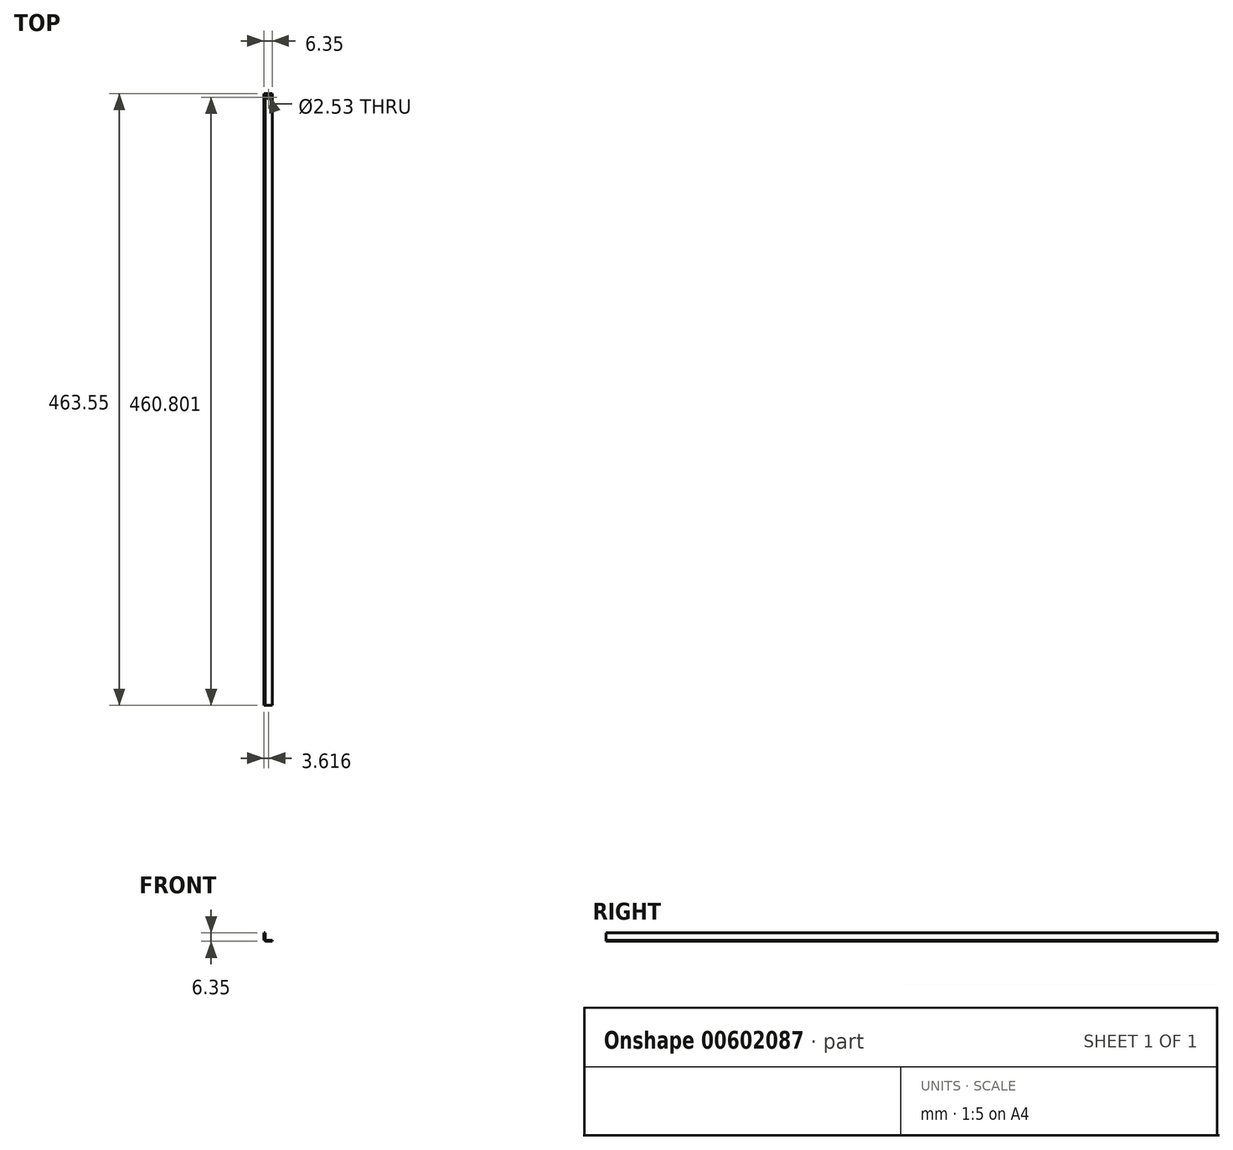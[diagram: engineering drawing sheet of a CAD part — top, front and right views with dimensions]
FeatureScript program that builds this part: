
annotation { "Feature Type Name" : "Feature", "Feature Type Description" : "" }
export const myFeature = defineFeature(function(context is Context, id is Id, definition is map)
    precondition{}
    {
        {
            var Q0;
            Q0=qCreatedBy(makeId("Front.planeOp"),FACE);
            var sketch = newSketch(context, id + "F0", { "sketchPlane" : qUnion([Q0])});
            skLineSegment(sketch, "E0.bottom", {"start": v(0, 0) * mm, "end": v(0.88, 0) * mm});
            skLineSegment(sketch, "E0.top", {"start": v(0, 6.35) * mm, "end": v(0.88, 6.35) * mm});
            skLineSegment(sketch, "E0.left", {"start": v(0, 0) * mm, "end": v(0, 6.35) * mm});
            skLineSegment(sketch, "E0.right", {"start": v(0.88, 0) * mm, "end": v(0.88, 6.35) * mm});
            skLineSegment(sketch, "E1.bottom", {"start": v(0, 0) * mm, "end": v(6.35, 0) * mm});
            skLineSegment(sketch, "E1.top", {"start": v(0, 0.81) * mm, "end": v(6.35, 0.81) * mm});
            skLineSegment(sketch, "E1.left", {"start": v(0, 0) * mm, "end": v(0, 0.81) * mm});
            skLineSegment(sketch, "E1.right", {"start": v(6.35, 0) * mm, "end": v(6.35, 0.81) * mm});
            skSolve(sketch);
        }
        {
            var Q0;
            {var subQ0=sQuery(id+"F0.wireOp",EDGE,"E0.top");Q0=makeQuery(id+"F0.imprint","IMPRINT",FACE,{"disambiguationData":[TD([[makeQuery(id+"F0.imprint","IMPRINT",EDGE,{"derivedFrom":subQ0}),-1.0]])]});}
            var Q1;
            {var subQ5=sQuery(id+"F0.wireOp",EDGE,"E1.right");Q1=makeQuery(id+"F0.imprint","IMPRINT",FACE,{"disambiguationData":[TD([[makeQuery(id+"F0.imprint","IMPRINT",EDGE,{"derivedFrom":subQ5}),1.0]])]});}
            var Q2;
            {var subQ5=sQuery(id+"F0.wireOp",EDGE,"E1.left");Q2=makeQuery(id+"F0.imprint","IMPRINT",FACE,{"disambiguationData":[TD([[makeQuery(id+"F0.imprint","IMPRINT",EDGE,{"derivedFrom":subQ5}),-1.0]])]});}
            extrude(context, id + "F1", {"entities" : qUnion([Q0, Q1, Q2]), "depth" : 463.55 * mm, "offsetDistance" : 25.4 * mm});
        }
        {
            var Q0;
            Q0=makeQuery(id+"F1.opExtrude","SWEPT_FACE",FACE,{"disambiguationData":[OSD([sQuery(id+"F0.wireOp",EDGE,"E1.top")])]});
            var sketch = newSketch(context, id + "F2", { "sketchPlane" : qUnion([Q0])});
            skLineSegment(sketch, "E2", {"start": v(0.88, 0) * mm, "end": v(3.62, 0) * mm});
            skLineSegment(sketch, "E3", {"start": v(0.88, 0) * mm, "end": v(0.88, -2.75) * mm});
            skCircle(sketch, "E4", {"center": v(3.62, -2.75) * mm, "radius": 1.26 * mm});
            skSolve(sketch);
        }
        {
            var Q0;
            Q0=makeQuery(id+"F2.imprint","IMPRINT",FACE,{"disambiguationData":[TD([[makeQuery(id+"F2.imprint","IMPRINT",EDGE,{"derivedFrom":sQuery(id+"F2.wireOp",EDGE,"E4")}),1.0]])]});
            extrude(context, id + "F3", {"entities" : qUnion([Q0]), "operationType" : NewBodyOperationType.REMOVE, "oppositeDirection" : true, "depth" : 25.4 * mm, "offsetDistance" : 25.4 * mm});
        }
        {
            var Q0;
            Q0=makeQuery(id+"F1.opExtrude","SWEPT_FACE",FACE,{"disambiguationData":[OSD([sQuery(id+"F0.wireOp",EDGE,"E1.top")])]});
            var sketch = newSketch(context, id + "F4", { "sketchPlane" : qUnion([Q0])});
            skLineSegment(sketch, "E5", {"start": v(6.35, -463.55) * mm, "end": v(6.35, -460.8) * mm});
            skCircle(sketch, "E6", {"center": v(3.62, -460.8) * mm, "radius": 1.28 * mm});
            skPoint(sketch, "E6.centerSnap0", {"position": v(3.62, -463.55) * mm});
            skSolve(sketch);
        }
        {
            var Q0;
            Q0=makeQuery(id+"F4.imprint","IMPRINT",FACE,{"disambiguationData":[TD([[makeQuery(id+"F4.imprint","IMPRINT",EDGE,{"derivedFrom":sQuery(id+"F4.wireOp",EDGE,"E6")}),1.0]])]});
            extrude(context, id + "F5", {"entities" : qUnion([Q0]), "operationType" : NewBodyOperationType.REMOVE, "oppositeDirection" : true, "depth" : 25.4 * mm, "offsetDistance" : 25.4 * mm});
        }
    });
